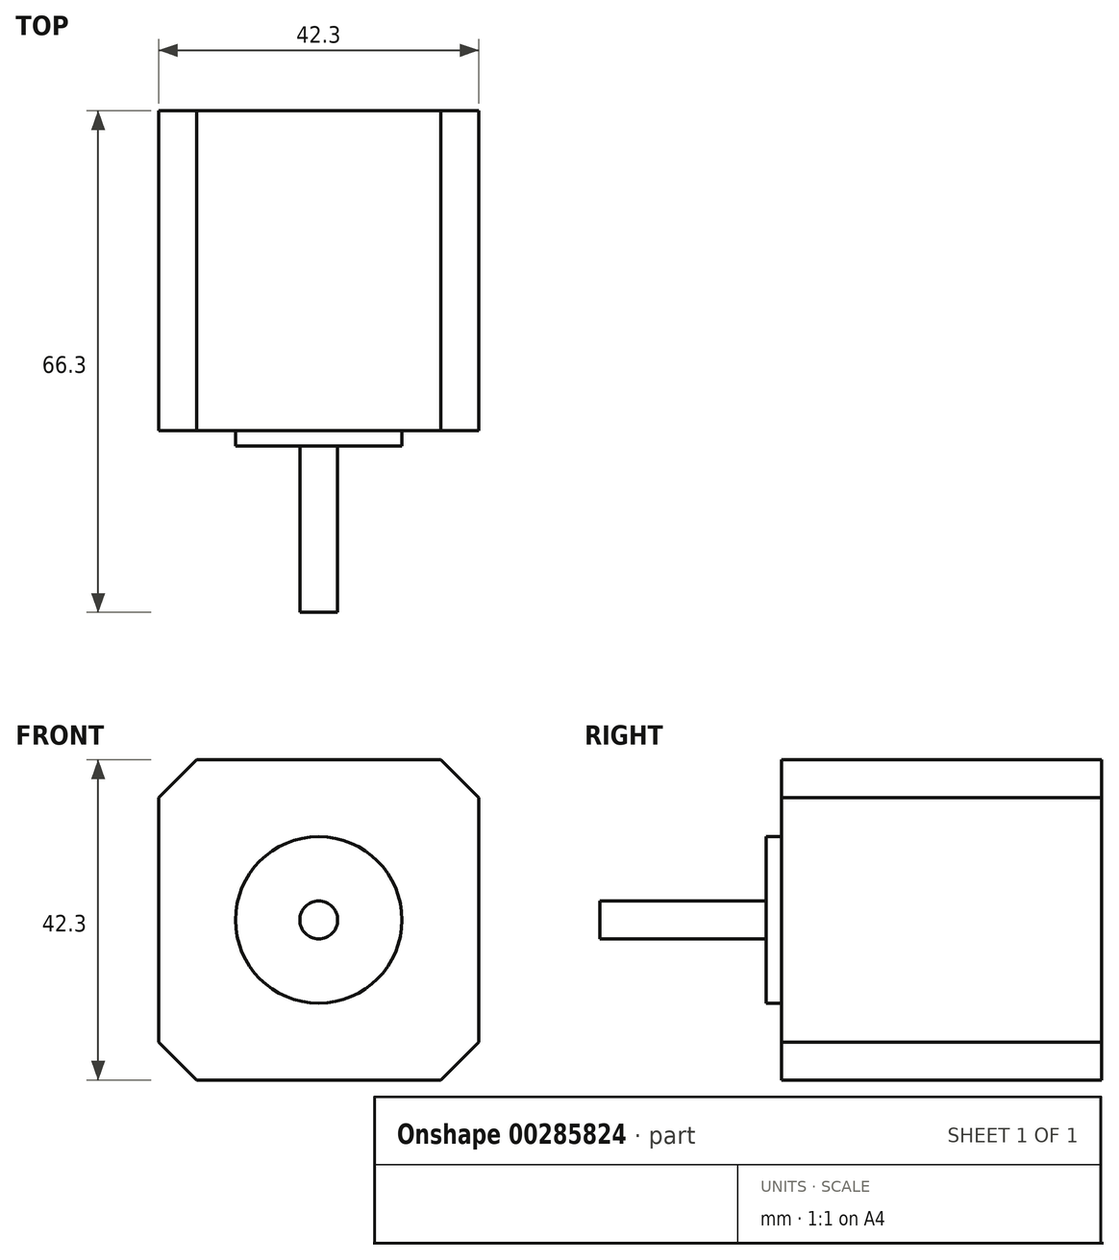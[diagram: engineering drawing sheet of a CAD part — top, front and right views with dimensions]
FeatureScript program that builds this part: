
annotation { "Feature Type Name" : "Feature", "Feature Type Description" : "" }
export const myFeature = defineFeature(function(context is Context, id is Id, definition is map)
    precondition{}
    {
        {
            var Q0;
            Q0=qCreatedBy(makeId("Front.planeOp"),FACE);
            var sketch = newSketch(context, id + "F0", { "sketchPlane" : qUnion([Q0])});
            skLineSegment(sketch, "E0.bottom", {"start": v(21.15, 21.15) * mm, "end": v(-21.15, 21.15) * mm});
            skLineSegment(sketch, "E0.top", {"start": v(21.15, -21.15) * mm, "end": v(-21.15, -21.15) * mm});
            skLineSegment(sketch, "E0.left", {"start": v(21.15, 21.15) * mm, "end": v(21.15, -21.15) * mm});
            skLineSegment(sketch, "E0.right", {"start": v(-21.15, 21.15) * mm, "end": v(-21.15, -21.15) * mm});
            skPoint(sketch, "E0.middle", {"position": v(0, 0) * mm});
            skSolve(sketch);
        }
        {
            var Q0;
            Q0 = qSketchRegion(id + "F0", true);
            extrude(context, id + "F1", {"entities" : qUnion([Q0]), "endBound" : BoundingType.SYMMETRIC, "depth" : 42.3 * mm});
        }
        {
            var Q0;
            Q0=makeQuery(id+"F1.opExtrude","SWEPT_EDGE",EDGE,{"disambiguationData":[OSD([sQuery(id+"F0.wireOp",EDGE,"E0.bottom"),sQuery(id+"F0.wireOp",EDGE,"E0.right")])]});
            var Q1;
            Q1=makeQuery(id+"F1.opExtrude","SWEPT_EDGE",EDGE,{"disambiguationData":[OSD([sQuery(id+"F0.wireOp",EDGE,"E0.bottom"),sQuery(id+"F0.wireOp",EDGE,"E0.left")])]});
            var Q2;
            Q2=makeQuery(id+"F1.opExtrude","SWEPT_EDGE",EDGE,{"disambiguationData":[OSD([sQuery(id+"F0.wireOp",EDGE,"E0.top"),sQuery(id+"F0.wireOp",EDGE,"E0.right")])]});
            var Q3;
            Q3=makeQuery(id+"F1.opExtrude","SWEPT_EDGE",EDGE,{"disambiguationData":[OSD([sQuery(id+"F0.wireOp",EDGE,"E0.top"),sQuery(id+"F0.wireOp",EDGE,"E0.left")])]});
            chamfer(context, id + "F2", {"entities" : qUnion([Q0, Q1, Q2, Q3]), "width" : 5 * mm, "tangentPropagation" : true});
        }
        {
            var Q0;
            Q0=makeQuery(id+"F1.opExtrude","CAP_FACE",FACE,{"disambiguationData":[OSD([sQuery(id+"F0.wireOp",EDGE,"E0.bottom"),sQuery(id+"F0.wireOp",EDGE,"E0.top"),sQuery(id+"F0.wireOp",EDGE,"E0.left"),sQuery(id+"F0.wireOp",EDGE,"E0.right")])],"isStart":false});
            var sketch = newSketch(context, id + "F3", { "sketchPlane" : qUnion([Q0])});
            skCircle(sketch, "E1", {"center": v(0, 0) * mm, "radius": 11 * mm});
            skSolve(sketch);
        }
        {
            var Q0;
            Q0 = qSketchRegion(id + "F3", true);
            extrude(context, id + "F4", {"entities" : qUnion([Q0]), "operationType" : NewBodyOperationType.ADD, "depth" : 2 * mm});
        }
        {
            var Q0;
            Q0=makeQuery(id+"F4.opExtrude","CAP_FACE",FACE,{"disambiguationData":[OSD([sQuery(id+"F3.wireOp",EDGE,"E1")])],"isStart":false});
            var sketch = newSketch(context, id + "F5", { "sketchPlane" : qUnion([Q0])});
            skCircle(sketch, "E2", {"center": v(0, 0) * mm, "radius": 2.5 * mm});
            skSolve(sketch);
        }
        {
            var Q0;
            Q0 = qSketchRegion(id + "F5", true);
            extrude(context, id + "F6", {"entities" : qUnion([Q0]), "operationType" : NewBodyOperationType.ADD, "depth" : 22 * mm});
        }
    });
